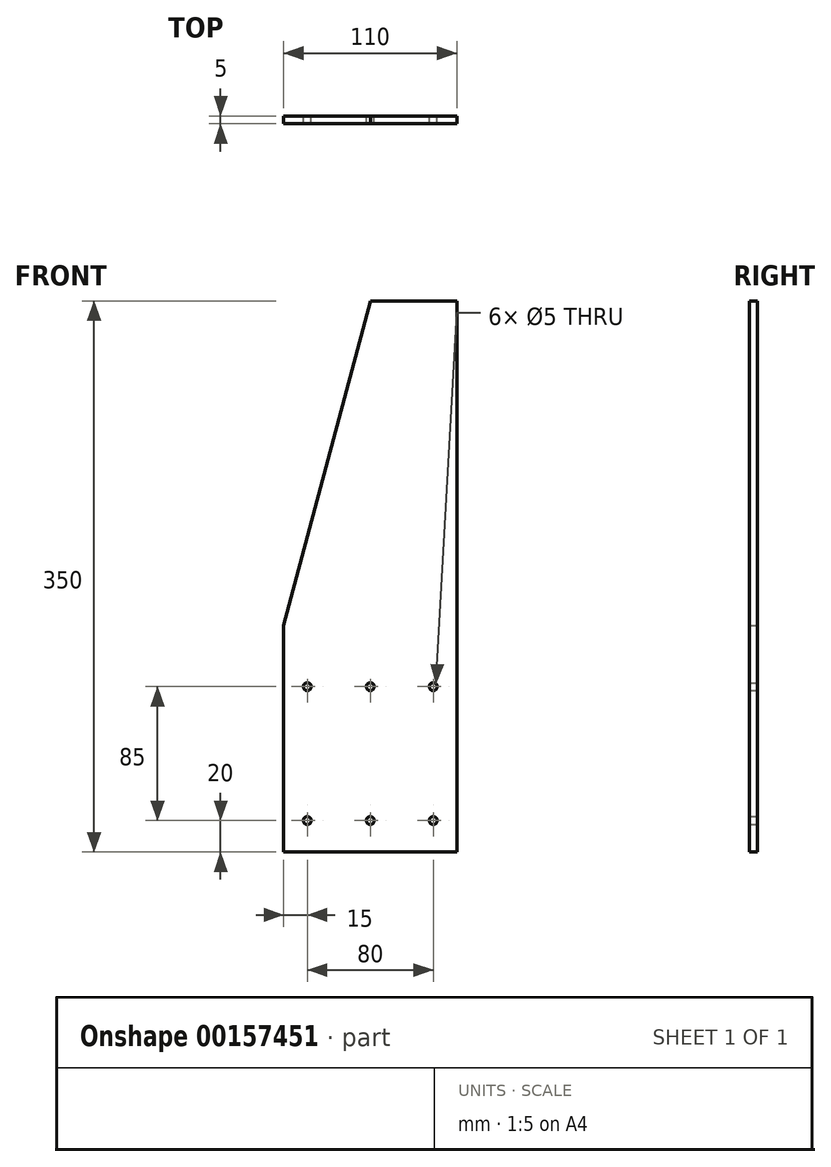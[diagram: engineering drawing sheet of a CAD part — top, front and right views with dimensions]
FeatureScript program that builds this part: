
annotation { "Feature Type Name" : "Feature", "Feature Type Description" : "" }
export const myFeature = defineFeature(function(context is Context, id is Id, definition is map)
    precondition{}
    {
        {
            var Q0;
            Q0=qCreatedBy(makeId("Front.planeOp"),FACE);
            var sketch = newSketch(context, id + "F0", { "sketchPlane" : qUnion([Q0])});
            skLineSegment(sketch, "E0.bottom", {"start": v(55, -175) * mm, "end": v(-55, -175) * mm});
            skLineSegment(sketch, "E0.top", {"start": v(55, 175) * mm, "end": v(0, 175) * mm});
            skLineSegment(sketch, "E0.left", {"start": v(55, -175) * mm, "end": v(55, 175) * mm});
            skLineSegment(sketch, "E0.right", {"start": v(-55, -175) * mm, "end": v(-55, -31.23) * mm});
            skPoint(sketch, "E0.middle", {"position": v(0, 0) * mm});
            skCircle(sketch, "E1", {"center": v(-40, -70) * mm, "radius": 2.5 * mm});
            skCircle(sketch, "E2", {"center": v(0, -70) * mm, "radius": 2.5 * mm});
            skCircle(sketch, "E3", {"center": v(-40, -155) * mm, "radius": 2.5 * mm});
            skCircle(sketch, "E4", {"center": v(0, -155) * mm, "radius": 2.5 * mm});
            skCircle(sketch, "E5", {"center": v(40, -155) * mm, "radius": 2.5 * mm});
            skCircle(sketch, "E6", {"center": v(40, -70) * mm, "radius": 2.5 * mm});
            skLineSegment(sketch, "E7", {"start": v(0, 175) * mm, "end": v(-55, -31.23) * mm});
            skPoint(sketch, "E8.orphan", {"position": v(-55, 175) * mm});
            skSolve(sketch);
        }
        {
            var Q0;
            Q0=makeQuery(id+"F0.imprint","IMPRINT",FACE,{"disambiguationData":[TD([[makeQuery(id+"F0.imprint","IMPRINT",EDGE,{"derivedFrom":sQuery(id+"F0.wireOp",EDGE,"E0.bottom")}),-1.0]])]});
            extrude(context, id + "F1", {"entities" : qUnion([Q0]), "depth" : 5 * mm});
        }
    });
